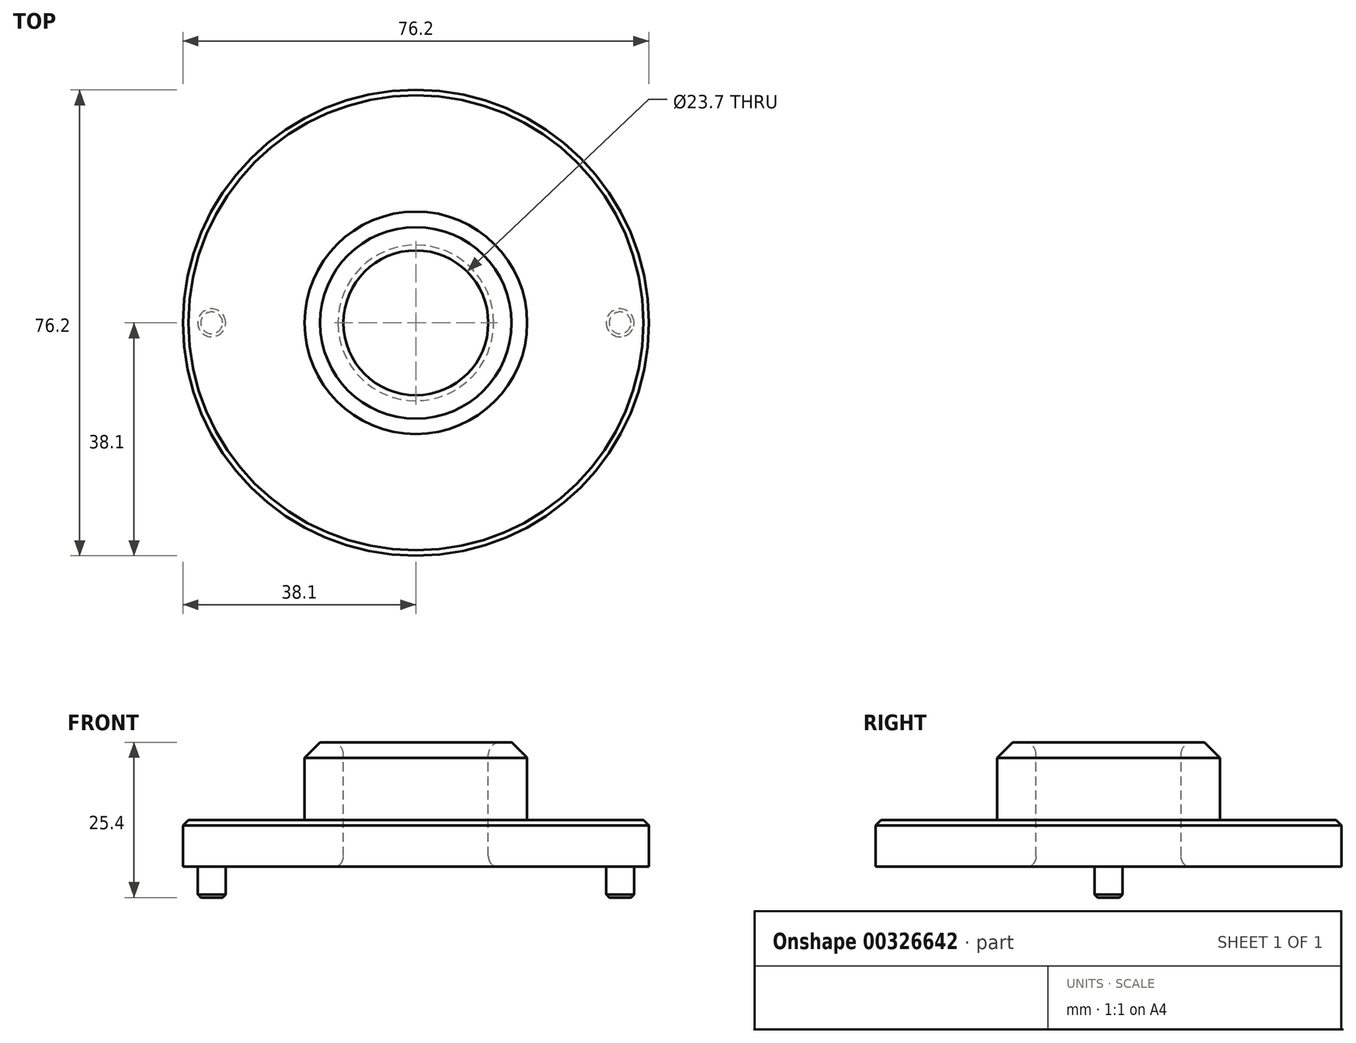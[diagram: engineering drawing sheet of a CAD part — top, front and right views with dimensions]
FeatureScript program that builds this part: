
annotation { "Feature Type Name" : "Feature", "Feature Type Description" : "" }
export const myFeature = defineFeature(function(context is Context, id is Id, definition is map)
    precondition{}
    {
        {
            var Q0;
            Q0=qCreatedBy(makeId("Top.planeOp"),FACE);
            var sketch = newSketch(context, id + "F0", { "sketchPlane" : qUnion([Q0])});
            skCircle(sketch, "E0", {"center": v(0, 0) * mm, "radius": 38.1 * mm});
            skSolve(sketch);
        }
        {
            var Q0;
            Q0=makeQuery(id+"F0.imprint","IMPRINT",FACE,{"disambiguationData":[TD([[makeQuery(id+"F0.imprint","IMPRINT",EDGE,{"derivedFrom":sQuery(id+"F0.wireOp",EDGE,"E0")}),1.0]])]});
            extrude(context, id + "F1", {"entities" : qUnion([Q0]), "depth" : 7.62 * mm});
        }
        {
            var Q0;
            Q0=makeQuery(id+"F1.opExtrude","CAP_FACE",FACE,{"disambiguationData":[OSD([sQuery(id+"F0.wireOp",EDGE,"E0")])],"isStart":false});
            var sketch = newSketch(context, id + "F2", { "sketchPlane" : qUnion([Q0])});
            skCircle(sketch, "E1", {"center": v(0, 0) * mm, "radius": 11.85 * mm});
            skSolve(sketch);
        }
        {
            var Q0;
            Q0=makeQuery(id+"F2.imprint","IMPRINT",FACE,{"disambiguationData":[TD([[makeQuery(id+"F2.imprint","IMPRINT",EDGE,{"derivedFrom":sQuery(id+"F2.wireOp",EDGE,"E1")}),1.0]])]});
            extrude(context, id + "F3", {"entities" : qUnion([Q0]), "operationType" : NewBodyOperationType.REMOVE, "endBound" : BoundingType.THROUGH_ALL, "oppositeDirection" : true, "depth" : 25.4 * mm});
        }
        {
            var Q0;
            Q0=makeQuery(id+"F1.opExtrude","CAP_EDGE",EDGE,{"disambiguationData":[OSD([sQuery(id+"F0.wireOp",EDGE,"E0")])],"isStart":false});
            var Q1;
            Q1=makeQuery(id+"F3.boolean.opBoolean","INTERSECT",EDGE,{"derivedFrom":[makeQuery(id+"F1.opExtrude","CAP_FACE",FACE,{"disambiguationData":[OSD([sQuery(id+"F0.wireOp",EDGE,"E0")])],"isStart":true}),makeQuery(id+"F3.opExtrude","SWEPT_FACE",FACE,{"disambiguationData":[OSD([sQuery(id+"F2.wireOp",EDGE,"E1")])]})]});
            chamfer(context, id + "F4", {"entities" : qUnion([Q0, Q1]), "width" : 0.89 * mm, "tangentPropagation" : true});
        }
        {
            var Q0;
            Q0=makeQuery(id+"F1.opExtrude","CAP_FACE",FACE,{"disambiguationData":[OSD([sQuery(id+"F0.wireOp",EDGE,"E0")])],"isStart":true});
            var sketch = newSketch(context, id + "F5", { "sketchPlane" : qUnion([Q0])});
            skCircle(sketch, "E2", {"center": v(-33.4, 0) * mm, "radius": 2.29 * mm});
            skCircle(sketch, "E3", {"center": v(33.4, 0) * mm, "radius": 2.29 * mm});
            skSolve(sketch);
        }
        {
            var Q0;
            Q0 = qSketchRegion(id + "F5", true);
            extrude(context, id + "F6", {"entities" : qUnion([Q0]), "operationType" : NewBodyOperationType.ADD, "depth" : 5.08 * mm});
        }
        {
            var Q0;
            Q0=makeQuery(id+"F6.opExtrude","CAP_EDGE",EDGE,{"disambiguationData":[OSD([sQuery(id+"F5.wireOp",EDGE,"E3")])],"isStart":false});
            var Q1;
            Q1=makeQuery(id+"F6.opExtrude","CAP_EDGE",EDGE,{"disambiguationData":[OSD([sQuery(id+"F5.wireOp",EDGE,"E2")])],"isStart":false});
            chamfer(context, id + "F7", {"entities" : qUnion([Q0, Q1]), "width" : 0.5 * mm, "tangentPropagation" : true});
        }
        {
            var Q0;
            Q0=makeQuery(id+"F1.opExtrude","CAP_FACE",FACE,{"disambiguationData":[OSD([sQuery(id+"F0.wireOp",EDGE,"E0")])],"isStart":false});
            var sketch = newSketch(context, id + "F8", { "sketchPlane" : qUnion([Q0])});
            skCircle(sketch, "E4", {"center": v(0, 0) * mm, "radius": 18.2 * mm});
            skSolve(sketch);
        }
        {
            var Q0;
            Q0=makeQuery(id+"F8.imprint","IMPRINT",FACE,{"disambiguationData":[TD([[makeQuery(id+"F8.imprint","IMPRINT",EDGE,{"derivedFrom":sQuery(id+"F8.wireOp",EDGE,"E4")}),1.0]])]});
            extrude(context, id + "F9", {"entities" : qUnion([Q0]), "operationType" : NewBodyOperationType.ADD, "depth" : 12.7 * mm});
        }
        {
            var Q0;
            {var subQ0=sQuery(id+"F2.wireOp",EDGE,"E1");Q0=makeQuery(id+"F9.boolean.opBoolean","MERGE",FACE,{"derivedFrom":[makeQuery(id+"F3.boolean.opBoolean","COPY",FACE,{"derivedFrom":makeQuery(id+"F3.opExtrude","SWEPT_FACE",FACE,{"disambiguationData":[OSD([subQ0])]})}),makeQuery(id+"F9.opExtrude","SWEPT_FACE",FACE,{"disambiguationData":[OSD([subQ0])]})]});}
            fillet(context, id + "F10", {"entities" : qUnion([Q0]), "radius" : 2.03 * mm, "tangentPropagation" : true, "allowEdgeOverflow" : false});
        }
        {
            var Q0;
            Q0=makeQuery(id+"F9.opExtrude","CAP_EDGE",EDGE,{"disambiguationData":[OSD([sQuery(id+"F8.wireOp",EDGE,"E4")])],"isStart":false});
            chamfer(context, id + "F11", {"entities" : qUnion([Q0]), "width" : 2.54 * mm, "tangentPropagation" : true});
        }
    });
